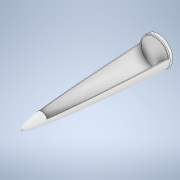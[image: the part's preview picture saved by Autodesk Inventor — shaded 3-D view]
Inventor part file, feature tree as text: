
AUTODESK INVENTOR PART (.ipt)
format: ipt  version: 2020.3 (Build 243373000, 373)  size: 286,720 bytes
history: native  units: mm
features: sketch x2, extrude x2, revolve x1
ambient origin geometry x8: Origin, YZ Plane, XZ Plane, XY Plane, X Axis, Y Axis, Z Axis, Center Point
bodies: Body1 (feature_tree)
feature tree (5):
  sketch  "Sketch2"  dims[d51=25.9mm d52=5.0mm]
  revolve  "Revolution5"  [1 undecoded]
  extrude  "Extrusion4"  Depth=2.0mm
  extrude  "Extrusion5"  Depth=25.9mm
  sketch  "Sketch3"  dims[d53=0.9mm d54=2.0mm d55=25.9mm d56=5.0mm d57=0.9mm d58=212.5mm d59=250.0mm d60=25.0mm d61=25.0mm d62=248.2mm d64=25.0mm d67=2.0mm d68=212.5mm d69=5.0mm d70=8.0mm d71=212.5mm d72=15.232132mm d73=360.0deg d74=60.0mm d75=0.0mm d76=3.0mm d77=5.0mm d78=30.0mm d79=0.0mm d7=0.5mm d8=0.872665mm d9=0.5mm d10=0.872665mm]
note: 1 required parameter value undecoded (feature->parameter linkage not recoverable at this tier; creation-order binding heuristic only, values carry confidence <= 0.55)
